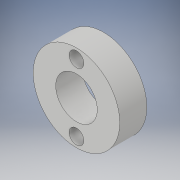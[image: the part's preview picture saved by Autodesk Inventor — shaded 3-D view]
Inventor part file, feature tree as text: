
AUTODESK INVENTOR PART (.ipt)
format: ipt  version: 2019 (Build 230136000, 136)  size: 149,504 bytes
history: native  units: in
note: dims shown in document units (in); Inventor stores cm internally (conversion verified against a paired STEP export)
features: extrude x3, sketch x3, plane x1
ambient origin geometry x8: Origin, YZ Plane, XZ Plane, XY Plane, X Axis, Y Axis, Z Axis, Center Point
bodies: Solid1 (feature_tree)
feature tree (7):
  plane  "Work Plane2"
  extrude  "Extrusion2"  Depth=0.136in
  extrude  "Extrusion4"  Depth=0.6185in
  extrude  "Extrusion5"  Depth=0.25in
  sketch  "Sketch3"  dims[d9=0.8in d10=0.136in]
  sketch  "Sketch4"  dims[d11=0.136in d12=0.6185in]
  sketch  "Sketch5"  dims[d13=0.3093in d14=0.384in d16=0.0in d17=0.25in d18=0.0in d26=0.3093in d27=0.45in d28=0.063in d29=0.0in d30=0.0625in d31=0.0625in d32=0.125in d33=0.125in d34=0.063in d35=0.0in]
